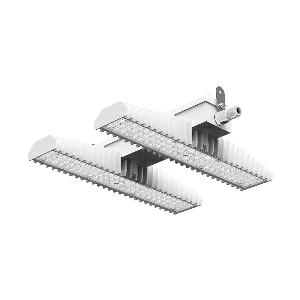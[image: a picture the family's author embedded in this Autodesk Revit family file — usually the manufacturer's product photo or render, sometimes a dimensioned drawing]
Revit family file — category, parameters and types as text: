
# Revit family: 3f_filippi_-_3f_lem_ho_medio_3f_filippi_-_58965_-_3f_lem_2_ho_led_140_cr_medio
name_source: partatom
category: Lighting Fixtures
units: mm (PartAtom-declared; Revit-internal decimal feet)

## family parameters
Cut with Voids When Loaded = No
Host = Face
Light Source = No
Part Type = Normal
Room Calculation Point = No
Round Connector Dimension = Use Diameter
Shared = No

## types (1)
- 3F Filippi - 3F LEM HO Medio (1 x LED, 22128 lm, 138 W, 4000 K)
    Apparent Load = 138 VA
    Approval mark = CE
    CIE Flux Codes = 83 96 99 100 100
    Color Rendering = 80
    Color Temperature = 4000 K
    Control Gear = Electronic ballast
    Default Elevation = 1800 mm
    Description = Industrial luminaire with high light output and high luminous efficiency designed with the most innovative technologies for environments with temperature up to 55°C.

ILLUMINOTECHNICAL
Luminous efficiency 100% (DLOR 100%, ULOR 0%).
Initial luminous flux of the luminaire 22128 lm.
Medium distribution with rectangular shape.
Installation Interdistance Transv.D = 1.17 x hu - Long.D = 1.21 x hu.
Tabular UGR (CIE 117 - 4H-8H; S=0.25H; 70/50/20): RUG 19.5 - 19.1.
Beam angle: 65° - 67°.
Luminous efficacy 160 lm/W.
Lifetime (L93/B10): 30000 h. (tq+25°C)
Lifetime (L90/B10): 50000 h. (tq+25°C)
Lifetime (L85/B10): 80000 h. (tq+25°C)
Lifetime (L80/B10): 100000 h. (tq+25°C)
Lifetime (L85/B10): 50000 h. (tq+55°C)
Sudden decreased luminous flux after 50000 hours: 0% (C0).
Photobiological safety in compliance with IEC/TR 62778: RG0 risk exempt, (IEC 62471).
In compliance with IEC/EN 62722-2-1 - IEC/EN 62717 standards.

SOURCE
2 Mid-Power linear LED modules 70W/840.
Energy efficiency class (UE 2019/2020 - UE 2019/2015): C.
CIE 13.3 Colour rendering index: CRI >80 (R9 <50%).
IES TM-30 Fidelity Index: Rf = 84 Rg = 95.
CCT nominal colour temperature 4000 K.
Colour initial tolerance (MacAdam): SDCM 3.

MECHANICAL
Passive modular heatsinks in die-casted aluminium, painted in white colour.
To optimize the thermal management of the LED module, the heatsinks are oversized and provided with self-cleaning of cooling fins.
Wiring body in aluminium and galvanised steel anchored solidly to the sinks and thermally separated.
3F Lens lenses with high luminous efficiency, transparent methacrylate (PMMA), fixed to the LED modules.
Fixing brackets in stainless steel.
Luminaire with limited surface temperature. - D - (EN 60598-2-24)
Dimensions: 470x542 mm, height 129 mm. Weight 9.09 kg.
IP65 protection degree.
Mechanical strength to impacts IK06 (1 joule).
Glow-wire test resistance 650°C.

ELECTRICAL
Halogen Free electronic wiring 230V-50/60Hz, power factor 0.97, THD <25%, constant output current, class I, 1 driver.
Power of the luminaire 138 W.
ENEC - CE.
SAFE FLICKER: PstLM=<1 and SVM=<0.4 (IEC TR 61547-1 and IEC TR 63158), to ensure a more comfortable and safe light.
Luminaire compliant with EN 60598-2-22 for power supply from a centralised emergency system CPSS (Central Power Supply System), not incorporated in the luminaire - high risk areas excluded. The default power and flux are 100% in AC and 100% in DC.
Ambient temperature from -30°C to +55°C.
Temperature class T6 max 85°C.
Quick connection via M20 3P connector with 9-13 mm tightening range.
Power unit positioned on a separate compartment by the LED module to ensure optimum temperatures of cabling components, to be inspectable and maintainable.
Relative humidity UR: <85%.

INSTALLATION
Ceiling / Suspended / Wall.
All accessories dedicated to this product are available on the Catalog and on our website www.3F-Filippi.com.

APPLICATIONS
In commercial environments, exhibition and industrial areas, stores, open areas.
Environments in which it is necessary a total protection against falling fragments (eg environments with foodstuffs or machines with moving parts or with extreme temperature changes), use luminaires with polycarbonate lenses.

WARNING
Fixture not suitable for cold stores with an ambient temperature <0°C and/or relative humidity >85%.
Luminaire designed for disposal/recycling at end-of-life.
Replaceable (LED only) light source by a professional. Replaceable control gear by a professional.
    Height = 129 mm
    Lamp = 1 x LED
    Lamp Light Flux = 22128 lm
    Lamp Power = 138 W
    Lamp count = 1
    Length = 470 mm
    Lifetime = 50000 h
    Luminous efficacy = 160 lm/W
    Manufacturer = 3F Filippi
    ModVariant = No
    Model = 3F Filippi - 58965 - 3F LEM 2 HO LED 140 CR MEDIO
    Mounting Place = Ceiling
    Mounting Type = Pendant
    Number of Poles = 1
    OnlyDefault = Yes
    Power Factor = 1
    Product Name = 3F Filippi - 3F LEM HO Medio
    Product group = pendant luminaire
    ProductGroupID = 9
    Protection Class = Protection class I
    Protection Degree = IP 65
    RLX_Detail_Level = 1
    RLX_Emergency_Light_Flux = 0 lm
    RLX_Emergency_Type = 0
    RLX_Emergency_Type_DB = No
    RlxData = <blob elided: 95713 chars, md5=3d333adc>
    Socket = socket
    Standby Power = 0 W
    System Light Flux = 22128 lm
    System Power = 138 W
    Type Comments = Product without accessories
    Type Image = 3f_filippi_-_lem_2.jpg
    URL = http://relux.com
    VarID = ---
    Voltage = 0 V
    Weight = 0.00 kg
    Width = 542 mm

## geometry (parser evidence)
native form markers: Blend x4, Sweep x13
no freeform markers — native parametric forms only
